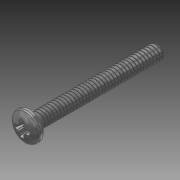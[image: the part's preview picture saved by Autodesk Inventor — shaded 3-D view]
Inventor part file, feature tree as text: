
AUTODESK INVENTOR PART (.ipt)
format: ipt  version: 2014 SP1 (Build 180222100, 222)  size: 1,016,832 bytes
history: native  units: in
note: dims shown in document units (in); Inventor stores cm internally (conversion verified against a paired STEP export)
features: fillet x1, other x1, imported_body x1
ambient origin geometry x8: Origin, YZ Plane, XZ Plane, XY Plane, X Axis, Y Axis, Z Axis, Center Point
bodies: Body1 (feature_tree)
feature tree (3):
  fillet  "Fillet1"  [1 undecoded]
  other  "91772A1151"
  imported_body  "Base1"
note: 1 required parameter value undecoded (feature->parameter linkage not recoverable at this tier; creation-order binding heuristic only, values carry confidence <= 0.55)
